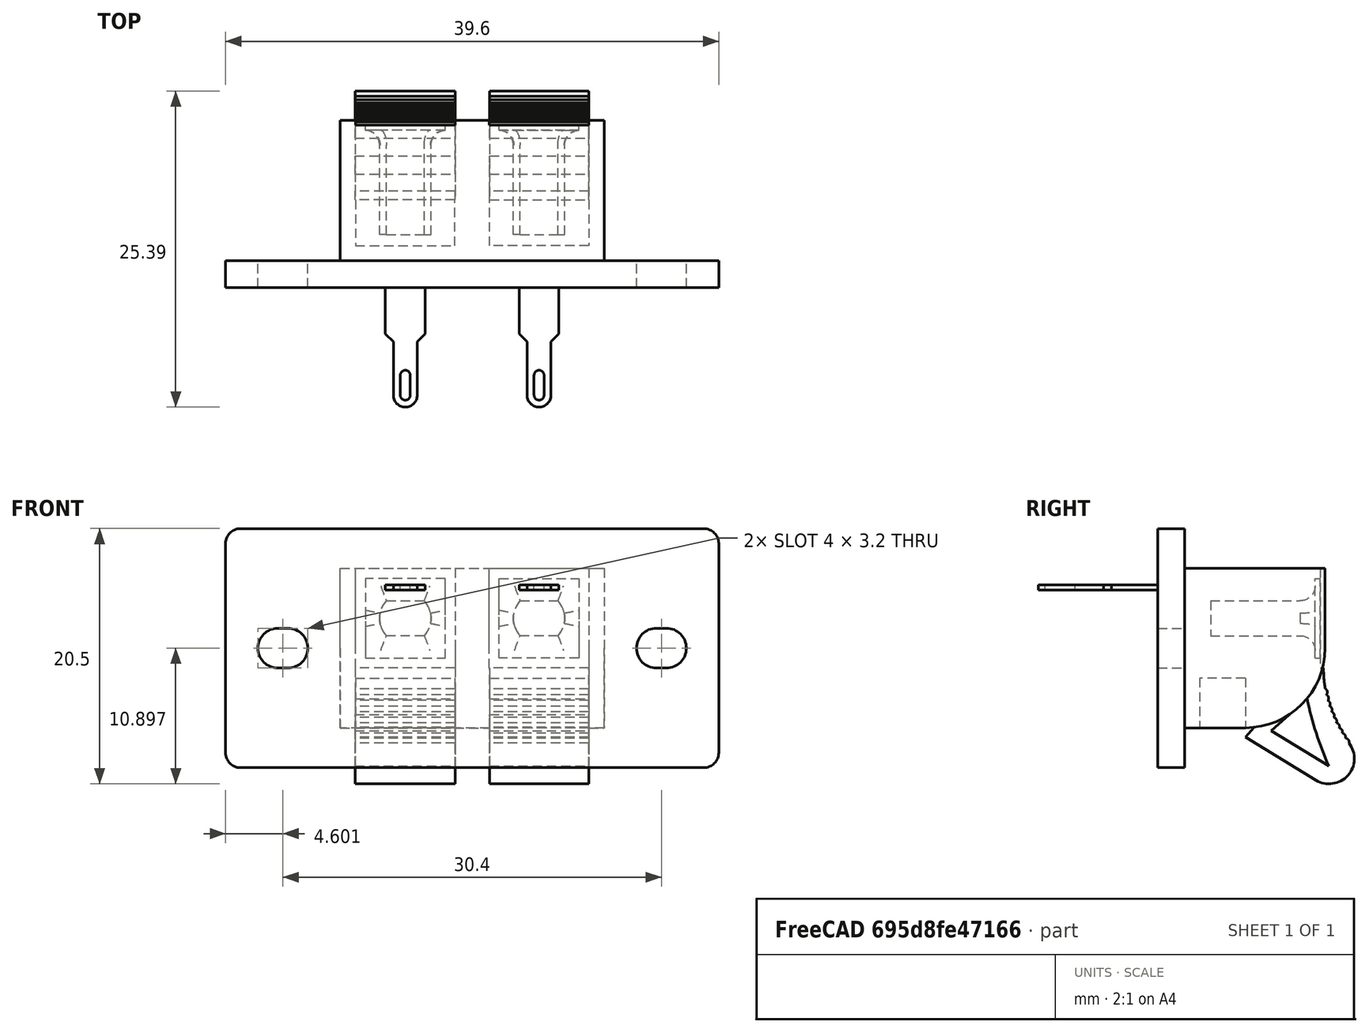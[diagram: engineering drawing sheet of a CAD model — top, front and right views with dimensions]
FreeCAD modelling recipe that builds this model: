
FCSTD DOCUMENT  (FreeCAD 0.19R24267 +148 (Git))
Label: bornier001
License: All rights reserved
LicenseURL: http://en.wikipedia.org/wiki/All_rights_reserved
objects: Part::Feature×1, Part::FeaturePython×1, Spreadsheet::Sheet×1, Sketcher::SketchObject×1, PartDesign::Body×1, App::Part×1
note: 4 computed .brp shape members not serialized (recipe doc carries the construction recipe); baked Part::Feature solids carry a one-line shape summary decoded from their .brp

FEATURE [Part::Feature] Part__Feature  label="Borne de haut parleur femelle 2 voies"
  shape: bbox 49.5 x 31.73 x 25.62 mm, 146 faces (baked)
FEATURE [Part::FeaturePython] Scale  # Draft clone (typed FeaturePython)
  Fuse = false
  Objects = -> [Part__Feature]
  Placement = pos=(-0.0194489,-1.2417e-07,-0.083234) rot=(0,0,1;0rad)
  Scale = (0.8,0.8,0.8)
FEATURE [Spreadsheet::Sheet] Spreadsheet  label="bornSp"
  cells = A2=bornierVisEntraxe; B2(bornierVisEntraxe)=29; A3=bornierVisTrouDiam; B3(bornierVisTrouDiam)=4; A4=bornirCosseEntreaxe; B4(bornirCosseEntreaxe)=12; A5=bornierCosseTrousDiam; B5(bornierCosseTrousDiam)=6; A6=bornierDistAxeVisAxeCosSurY; B6(bornierDistAxeVisAxeCosSurY)=5.5; C6=Sur X centré
FEATURE [Sketcher::SketchObject] Sketch001
  FullyConstrained = true
  MapMode = 5
  Placement = pos=(0,0,0) rot=(1,0,0;1.5708rad)
  Support = -> [XZ_Plane001]
  expr: Constraints[15] = <<bornSp>>.bornierDistAxeVisAxeCosSurY
  expr: Constraints[11] = <<bornSp>>.bornierVisEntraxe
  expr: Constraints[10] = <<bornSp>>.bornierVisTrouDiam
  expr: Constraints[9] = <<bornSp>>.bornirCosseEntreaxe
  expr: Constraints[8] = <<bornSp>>.bornierCosseTrousDiam
  sketch-geometry (7):
    g0: Circle CenterX=-6 CenterY=5.5 CenterZ=0 NormalX=0 NormalY=0 NormalZ=1 AngleXU=0 Radius=3
    g1: Circle CenterX=6 CenterY=5.5 CenterZ=0 NormalX=0 NormalY=0 NormalZ=1 AngleXU=0 Radius=3
    g2: Circle CenterX=-14.5 CenterY=0 CenterZ=0 NormalX=0 NormalY=0 NormalZ=1 AngleXU=0 Radius=2
    g3: Circle CenterX=14.5 CenterY=0 CenterZ=0 NormalX=0 NormalY=0 NormalZ=1 AngleXU=0 Radius=2
    g4: LineSegment StartX=-6 StartY=5.5 StartZ=0 EndX=6 EndY=5.5 EndZ=0
    g5: LineSegment StartX=-14.5 StartY=0 StartZ=0 EndX=14.5 EndY=0 EndZ=0
    g6: LineSegment StartX=0 StartY=0 StartZ=0 EndX=0 EndY=5.5 EndZ=0
  constraints (17):
    c: Equal(g2,g3)
    c: Equal(g0,g1)
    c: Coincident(g4,g0)
    c: Coincident(g4,g1)
    c: Horizontal(g4)
    c: Coincident(g5,g2)
    c: Coincident(g5,g3)
    c: Horizontal(g5)
    c: Diameter(g1) = 6
    c: DistanceX(g4,g4) = 12
    c: Diameter(g3) = 4
    c: DistanceX(g5,g5) = 29
    c: Vertical(g6)
    c: Symmetric(g2,g3,g6)
    c: Symmetric(g0,g1,g6)
    c: DistanceY(g6,g6) = 5.5
    c: Coincident(g6,g-1)
FEATURE [PartDesign::Body] Body
  Group = -> [Sketch001]
  Origin = -> Origin001
FEATURE [App::Part] Part  label="bornier"
  Group = -> [Body,Part__Feature,Scale,Spreadsheet]
  Origin = -> Origin
